# Revit family: 101010005202804
name_source: partatom
category: Modelos genéricos
revit_build: Autodesk Revit 2018 (Build: 20190510_1515(x64)
units: mm (PartAtom-declared; Revit-internal decimal feet)

## family parameters
Compartido = No
Corte con vacíos al cargar = No
Cota de conector redondo = Diámetro de uso
Puede alojar armadura = No
Punto de cálculo de habitación = No
Se basa en plano de trabajo = No
Siempre vertical = No
Tipo de pieza = Normal

## types (1)
- SEPARADOR MOLDAJE CONO 5/8" BOLSA 1.000UN
    Aplicacion = Para instalar el cono 5/8 se necesita un tubo de PVC para proteger el tornillo pasante y unir los conos. Para un tabique de espesor 30cm hay que cortar los tubos a 28cm.
    Color = Negro
    Descripción = Se usa en la fabricación de tabique, columnas, vigas altas y losas de hormigón armado. Evita irregularidades en los espesores de los mismos.
    Dimension = 0.03 m
    Empresa = CNP SPA.
    Espesor = 0 m
    Material = PEAD
    Modelo = SEPARADOR MOLDAJE CONO 5/8"
    Nombre SKU = SEPARADOR MOLDAJE CONO 5/8" BOLSA 1.000UN
    Num SKUs = 101010005202804
    URL = https://www.empresascnp.cl
    Unidad = Bolsa 1000 Un.
    Url Ficha tecnica = https://empresascnp.cl
    Uso = Se usa en la fabricación de tabique, columnas, vigas altas y losas de hormigón armado. Evita irregularidades en los espesores de los mismos.
    Ventajas = Fácil de instalar, permite un perfecto acabado, economiza M.O. evita perdida de hormigón y previene la deformación del encofrado.

## geometry (parser evidence)
native form markers: Sweep x2
no freeform markers — native parametric forms only
